# Revit family: 935550001_Sifon Botella Ahorraespacio
name_source: partatom
category: Plumbing Fixtures
units: mm (PartAtom-declared; Revit-internal decimal feet)

## family parameters
Always vertical = Yes
Cut with Voids When Loaded = No
OmniClass Number = 23.27.43.00
OmniClass Title = Pipe Fittings
Part Type = Normal
Room Calculation Point = No
Round Connector Dimension = Use Diameter
Shared = No
Work Plane-Based = No

## types (1)
- 935550001_Sifon Botella Ahorraespacio
    Alto = 366 mm
    Creado por = BIMBAU
    Default Elevation = 0 mm  [stored 0 ft]
    Description = Para la fabricación de este producto se utilizan materiales, equipos y 
tecnologías de última generación, que permiten ofrecer un artículo con 
los más altos estándares de calidad.
    Fecha de creación = 09/04/2021
    Longitud = 322 mm  [stored 1.05643 ft]
    Manufacturer = Grival
    Material = Corona_Plastico_Blanco
    Model = Sifon Botella Ahorraespacio
    Normatividad = NTC 5302
    Recubrimientos = -Resistente a la corrosión, pelado y decoloración por agua. -Resistente al efecto de jabones y limpiadores de tocador. -Recubrimientos no tóxico. -Condición de servicio recomendada, uso domestico.
    Referencia = 935550001
    URL = https://www.grival.com

note: [stored X ft] marks values corroborated as IEEE doubles in the binary element streams (Revit-internal decimal feet)

## geometry (parser evidence)
native form markers: Sweep x5
no freeform markers — native parametric forms only
